FCSTD DOCUMENT  (FreeCAD 0.14R3702 (Git))
Label: battery-holder-8-AAA
License: CC-BY 3.0
LicenseURL: http://creativecommons.org/licenses/by/3.0/
objects: Part::Feature×54, Sketcher::SketchObject×25, PartDesign::Pocket×14, Part::Sweep×13, Part::Part2DObjectPython×11, Part::Compound×9, PartDesign::Pad×7, Part::MultiFuse×7, App::DocumentObjectGroup×6, Part::Mirroring×5, Part::Chamfer×4, Part::Fillet×1, PartDesign::Revolution×1, Part::Helix×1
note: 174 computed .brp shape members not serialized (recipe doc carries the construction recipe); baked Part::Feature solids carry a one-line shape summary decoded from their .brp

FEATURE [Sketcher::SketchObject] Sketch  label="battery-pack-left-body-1-sketch"
  Placement = pos=(0,0,0) rot=(1,0,0;1.5708rad)
  sketch-geometry (5):
    g0: LineSegment StartX=-19.65 StartY=11.95 StartZ=0 EndX=0 EndY=11.95 EndZ=0
    g1: LineSegment StartX=0 StartY=0 StartZ=0 EndX=-25.15 EndY=0 EndZ=0
    g2: LineSegment StartX=-25.15 StartY=0 StartZ=0 EndX=-25.15 EndY=6.45 EndZ=0
    g3: ArcOfCircle CenterX=-19.65 CenterY=6.45 CenterZ=0 NormalX=0 NormalY=0 NormalZ=1 Radius=5.5 StartAngle=1.5708 EndAngle=3.14159
    g4: LineSegment StartX=0 StartY=11.95 StartZ=0 EndX=0 EndY=0 EndZ=0
  constraints (15):
    c: Coincident(g1,g2)
    c: Horizontal(g0)
    c: Horizontal(g1)
    c: Vertical(g2)
    c: Tangent(g0,g3)
    c: Tangent(g2,g3)
    c: DistanceX(g1) = -25.15
    c: Radius(g3) = 5.5
    c: DistanceY(g-1,g0) = 11.95
    c: PointOnObject(g0,g-2)
    c: PointOnObject(g1,g-1)
    c: Coincident(g1,g-1)
    c: Vertical(g4)
    c: Coincident(g4,g0)
    c: Coincident(g4,g-1)
FEATURE [PartDesign::Pad] Pad  label="battery-pack-left-body-1"
  Length = 53.3
  Length2 = 100
  Midplane = true
  Placement = pos=(0,0,0) rot=(1,0,0;1.5708rad)
  Sketch = -> Sketch
  Type = 0
FEATURE [Sketcher::SketchObject] Sketch001  label="battery-pack-left-body-2-sketch"
  ExternalGeometry = -> [Pad]
  Placement = pos=(0,0,11.95) rot=(0,0,1;3.14159rad)
  Support = -> Pad [Face1]
  sketch-geometry (21):
    g0: LineSegment StartX=0.575 StartY=24.85 StartZ=0 EndX=11.6875 EndY=24.85 EndZ=0
    g1: LineSegment StartX=11.6875 StartY=24.85 StartZ=0 EndX=11.6875 EndY=-24.85 EndZ=0
    g2: LineSegment StartX=11.6875 StartY=-24.85 StartZ=0 EndX=0.575 EndY=-24.85 EndZ=0
    g3: LineSegment StartX=0.575 StartY=-24.85 StartZ=0 EndX=0.575 EndY=24.85 EndZ=0
    g4: LineSegment StartX=12.8375 StartY=24.85 StartZ=0 EndX=23.95 EndY=24.85 EndZ=0
    g5: LineSegment StartX=23.95 StartY=24.85 StartZ=0 EndX=23.95 EndY=22.75 EndZ=0
    g6: LineSegment StartX=23.95 StartY=-24.85 StartZ=0 EndX=12.8375 EndY=-24.85 EndZ=0
    g7: LineSegment StartX=12.8375 StartY=-24.85 StartZ=0 EndX=12.8375 EndY=24.85 EndZ=0
    g8: LineSegment [constr] StartX=12.2625 StartY=24.85 StartZ=0 EndX=12.2625 EndY=-24.85 EndZ=0
    g9: LineSegment StartX=22.75 StartY=22.75 StartZ=0 EndX=23.95 EndY=22.75 EndZ=0
    g10: LineSegment StartX=21.55 StartY=21.55 StartZ=0 EndX=21.55 EndY=10.15 EndZ=0
    g11: LineSegment StartX=22.75 StartY=8.95 StartZ=0 EndX=23.95 EndY=8.95 EndZ=0
    g12: LineSegment StartX=23.95 StartY=8.95 StartZ=0 EndX=23.95 EndY=-8.95 EndZ=0
    g13: ArcOfCircle CenterX=22.75 CenterY=21.55 CenterZ=0 NormalX=0 NormalY=0 NormalZ=1 Radius=1.2 StartAngle=1.5708 EndAngle=3.14159
    g14: ArcOfCircle CenterX=22.75 CenterY=10.15 CenterZ=0 NormalX=0 NormalY=0 NormalZ=1 Radius=1.2 StartAngle=3.14159 EndAngle=4.71239
    g15: LineSegment StartX=23.95 StartY=-8.95 StartZ=0 EndX=22.75 EndY=-8.95 EndZ=0
    g16: LineSegment StartX=21.55 StartY=-10.15 StartZ=0 EndX=21.55 EndY=-21.55 EndZ=0
    g17: LineSegment StartX=22.75 StartY=-22.75 StartZ=0 EndX=23.95 EndY=-22.75 EndZ=0
    g18: LineSegment StartX=23.95 StartY=-22.75 StartZ=0 EndX=23.95 EndY=-24.85 EndZ=0
    g19: ArcOfCircle CenterX=22.75 CenterY=-10.15 CenterZ=0 NormalX=0 NormalY=0 NormalZ=1 Radius=1.2 StartAngle=1.5708 EndAngle=3.14159
    g20: ArcOfCircle CenterX=22.75 CenterY=-21.55 CenterZ=0 NormalX=0 NormalY=0 NormalZ=1 Radius=1.2 StartAngle=3.14159 EndAngle=4.71239
  constraints (57):
    c: Coincident(g0,g1)
    c: Coincident(g1,g2)
    c: Coincident(g2,g3)
    c: Coincident(g3,g0)
    c: Horizontal(g0)
    c: Horizontal(g2)
    c: Vertical(g1)
    c: Vertical(g3)
    c: Coincident(g4,g5)
    c: Coincident(g18,g6)
    c: Coincident(g6,g7)
    c: Coincident(g7,g4)
    c: Horizontal(g4)
    c: Horizontal(g6)
    c: Vertical(g5)
    c: Vertical(g7)
    c: PointOnObject(g0,g4)
    c: Symmetric(g0,g2,g-1)
    c: PointOnObject(g1,g6)
    c: DistanceX(g-1,g0) = 0.575
    c: DistanceY(g0,g-3) = 1.8
    c: DistanceX(g4,g-4) = 1.2
    c: DistanceX(g0,g4) = 1.15
    c: PointOnObject(g8,g0)
    c: PointOnObject(g8,g2)
    c: Symmetric(g0,g4,g8)
    c: Symmetric(g0,g4,g8)
    c: Horizontal(g9)
    c: Vertical(g10)
    c: Horizontal(g11)
    c: Coincident(g5,g9)
    c: Coincident(g12,g11)
    c: Tangent(g5,g12)
    c: Tangent(g9,g13)
    c: Tangent(g10,g13)
    c: Radius(g13) = 1.2
    c: DistanceX(g10,g5) = 2.4
    c: Tangent(g10,g14)
    c: Tangent(g11,g14)
    c: Equal(g13,g14)
    c: Horizontal(g15)
    c: Vertical(g16)
    c: Horizontal(g17)
    c: Coincident(g12,g15)
    c: Coincident(g18,g17)
    c: Tangent(g12,g18)
    c: Tangent(g15,g19)
    c: Tangent(g16,g19)
    c: Tangent(g16,g20)
    c: Tangent(g17,g20)
    c: Equal(g19,g20)
    c: Equal(g20,g14)
    c: PointOnObject(g16,g10)
    c: Symmetric(g12,g11,g-1)
    c: Symmetric(g17,g5,g-1)
    c: DistanceY(g5) = -2.1
    c: DistanceY(g5,g11) = -13.8
FEATURE [PartDesign::Pocket] Pocket  label="battery-pack-left-body-2"
  Length = 10.5
  Placement = pos=(0,0,0) rot=(1,0,0;1.5708rad)
  Sketch = -> Sketch001
  Type = 0
FEATURE [Sketcher::SketchObject] Sketch002  label="left-body-3-sketch"
  ExternalGeometry = -> [Pocket]
  Placement = pos=(0,-22.75,0) rot=(1,0,0;1.5708rad)
  Support = -> Pocket [Face16]
  sketch-geometry (5):
    g0: ArcOfCircle CenterX=-15.7317 CenterY=4.18544 CenterZ=0 NormalX=0 NormalY=0 NormalZ=1 Radius=8.864 StartAngle=2.28682 EndAngle=2.75753
    g1: LineSegment [constr] StartX=-23.95 StartY=9.87929 StartZ=0 EndX=-23.95 EndY=7.50669 EndZ=0
    g2: LineSegment StartX=-23.95 StartY=7.50669 StartZ=0 EndX=-23.95 EndY=1.45 EndZ=0
    g3: LineSegment StartX=-23.95 StartY=1.45 StartZ=0 EndX=-21.55 EndY=1.45 EndZ=0
    g4: LineSegment StartX=-21.55 StartY=1.45 StartZ=0 EndX=-21.55 EndY=10.8726 EndZ=0
  constraints (13):
    c: PointOnObject(g0,g-5)
    c: Vertical(g1)
    c: Coincident(g1,g-4)
    c: Coincident(g0,g1)
    c: Vertical(g2)
    c: Coincident(g2,g3)
    c: Horizontal(g3)
    c: Coincident(g3,g4)
    c: Vertical(g4)
    c: Coincident(g4,g0)
    c: Coincident(g3,g-5)
    c: Coincident(g2,g-3)
    c: Coincident(g2,g0)
FEATURE [PartDesign::Pocket] Pocket001  label="left-body-3"
  Length = 47
  Placement = pos=(0,0,0) rot=(1,0,0;1.5708rad)
  Sketch = -> Sketch002
  Type = 0
FEATURE [Sketcher::SketchObject] Sketch003  label="left-body-4-sketch"
  ExternalGeometry = -> [Pocket001]
  Placement = pos=(-25.15,0,0) rot=(0.707107,0,-0.707107;3.14159rad)
  Support = -> Pocket001 [Face14]
  sketch-geometry (13):
    g0: LineSegment StartX=-9.87929 StartY=24.85 StartZ=0 EndX=-7.8 EndY=24.85 EndZ=0
    g1: LineSegment StartX=-6.9 StartY=23.95 StartZ=0 EndX=-6.9 EndY=23.65 EndZ=0
    g2: LineSegment StartX=-7.8 StartY=22.75 StartZ=0 EndX=-9.87929 EndY=22.75 EndZ=0
    g3: LineSegment StartX=-9.87929 StartY=22.75 StartZ=0 EndX=-9.87929 EndY=24.85 EndZ=0
    g4: ArcOfCircle CenterX=-7.8 CenterY=23.95 CenterZ=0 NormalX=0 NormalY=0 NormalZ=1 Radius=0.9 StartAngle=0 EndAngle=1.5708
    g5: ArcOfCircle CenterX=-7.8 CenterY=23.65 CenterZ=0 NormalX=0 NormalY=0 NormalZ=1 Radius=0.9 StartAngle=4.71239 EndAngle=6.28319
    g6: LineSegment StartX=-9.87929 StartY=-22.75 StartZ=0 EndX=-7.8 EndY=-22.75 EndZ=0
    g7: LineSegment StartX=-6.9 StartY=-23.65 StartZ=0 EndX=-6.9 EndY=-23.95 EndZ=0
    g8: LineSegment StartX=-7.8 StartY=-24.85 StartZ=0 EndX=-9.87929 EndY=-24.85 EndZ=0
    g9: LineSegment StartX=-9.87929 StartY=-24.85 StartZ=0 EndX=-9.87929 EndY=-22.75 EndZ=0
    g10: ArcOfCircle CenterX=-7.8 CenterY=-23.65 CenterZ=0 NormalX=0 NormalY=0 NormalZ=1 Radius=0.9 StartAngle=0 EndAngle=1.5708
    g11: ArcOfCircle CenterX=-7.8 CenterY=-23.95 CenterZ=0 NormalX=0 NormalY=0 NormalZ=1 Radius=0.9 StartAngle=4.71239 EndAngle=6.28319
    g12: LineSegment StartX=-6.45 StartY=7.15 StartZ=0 EndX=-6.45 EndY=-7.15002 EndZ=0
  constraints (32):
    c: Coincident(g2,g3)
    c: Coincident(g3,g0)
    c: Horizontal(g0)
    c: Horizontal(g2)
    c: Vertical(g1)
    c: Vertical(g3)
    c: Coincident(g0,g-3)
    c: Coincident(g2,g-3)
    c: Tangent(g0,g4)
    c: Tangent(g1,g4)
    c: Tangent(g1,g5)
    c: Tangent(g2,g5)
    c: Equal(g5,g4)
    c: Radius(g4) = 0.9
    c: DistanceX(g1,g-4) = 6.9
    c: PointOnObject(g12,g-5)
    c: Coincident(g8,g9)
    c: Coincident(g9,g6)
    c: Horizontal(g6)
    c: Horizontal(g8)
    c: Vertical(g7)
    c: Vertical(g9)
    c: Coincident(g6,g-6)
    c: Coincident(g8,g-6)
    c: Tangent(g6,g10)
    c: Tangent(g7,g10)
    c: Tangent(g7,g11)
    c: Tangent(g8,g11)
    c: Equal(g11,g10)
    c: Radius(g10) = 0.9
    c: PointOnObject(g7,g1)
    c: Vertical(g12)
FEATURE [PartDesign::Pocket] Pocket002  label="left-body-4"
  Length = 5
  Placement = pos=(0,0,0) rot=(1,0,0;1.5708rad)
  Sketch = -> Sketch003
  Type = 0
FEATURE [Sketcher::SketchObject] Sketch004  label="left-body-5-sketch"
  ExternalGeometry = -> [Pocket002]
  Placement = pos=(-25.15,0,0) rot=(0.707107,0,-0.707107;3.14159rad)
  Support = -> Pocket002 [Face12]
  sketch-geometry (6):
    g0: LineSegment StartX=-9.87929 StartY=8.95 StartZ=0 EndX=-8.25 EndY=8.95 EndZ=0
    g1: LineSegment StartX=-6.45 StartY=7.15 StartZ=0 EndX=-6.45 EndY=-7.15 EndZ=0
    g2: LineSegment StartX=-8.25 StartY=-8.95 StartZ=0 EndX=-9.87929 EndY=-8.95 EndZ=0
    g3: LineSegment StartX=-9.87929 StartY=-8.95 StartZ=0 EndX=-9.87929 EndY=8.95 EndZ=0
    g4: ArcOfCircle CenterX=-8.25 CenterY=7.15 CenterZ=0 NormalX=0 NormalY=0 NormalZ=1 Radius=1.8 StartAngle=0 EndAngle=1.5708
    g5: ArcOfCircle CenterX=-8.25 CenterY=-7.15 CenterZ=0 NormalX=0 NormalY=0 NormalZ=1 Radius=1.8 StartAngle=4.71239 EndAngle=6.28319
  constraints (15):
    c: Coincident(g2,g3)
    c: Coincident(g3,g0)
    c: Horizontal(g0)
    c: Horizontal(g2)
    c: Vertical(g1)
    c: Vertical(g3)
    c: Tangent(g0,g4)
    c: Tangent(g1,g4)
    c: Tangent(g1,g5)
    c: Tangent(g2,g5)
    c: Equal(g4,g5)
    c: Radius(g4) = 1.8
    c: PointOnObject(g1,g-3)
    c: Coincident(g0,g-4)
    c: Coincident(g2,g-4)
FEATURE [PartDesign::Pocket] Pocket003  label="left-body-5"
  Length = 5
  Midplane = true
  Placement = pos=(0,0,0) rot=(1,0,0;1.5708rad)
  Sketch = -> Sketch004
  Type = 0
FEATURE [Sketcher::SketchObject] Sketch005  label="left-body-6-sketch"
  ExternalGeometry = -> [Pocket003]
  Placement = pos=(-12.8375,0,0) rot=(0.707107,0,-0.707107;3.14159rad)
  Support = -> Pocket003 [Face7]
  sketch-geometry (4):
    g0: LineSegment StartX=-11.95 StartY=24.85 StartZ=0 EndX=-11.95 EndY=-24.85 EndZ=0
    g1: LineSegment StartX=-11.95 StartY=24.85 StartZ=0 EndX=-4.45 EndY=6.35 EndZ=0
    g2: LineSegment StartX=-4.45 StartY=6.35 StartZ=0 EndX=-4.45 EndY=-6.35 EndZ=0
    g3: LineSegment StartX=-4.45 StartY=-6.35 StartZ=0 EndX=-11.95 EndY=-24.85 EndZ=0
  constraints (11):
    c: Vertical(g0)
    c: Coincident(g1,g-3)
    c: Coincident(g1,g2)
    c: Vertical(g2)
    c: Coincident(g2,g3)
    c: Coincident(g3,g-3)
    c: Symmetric(g2,g1,g-1)
    c: DistanceX(g1,g-4) = 3
    c: DistanceY(g-4,g1) = -18.5
    c: Coincident(g0,g1)
    c: Coincident(g0,g3)
FEATURE [PartDesign::Pocket] Pocket004  label="left-body-6"
  Length = 5
  Placement = pos=(0,0,0) rot=(1,0,0;1.5708rad)
  Sketch = -> Sketch005
  Type = 1
FEATURE [Sketcher::SketchObject] Sketch006  label="left-body-7-sketch"
  ExternalGeometry = -> [Pocket004]
  Placement = pos=(0,-26.65,0) rot=(1,0,0;1.5708rad)
  Support = -> Pocket004 [Face11]
  sketch-geometry (4):
    g0: LineSegment [constr] StartX=-18.3937 StartY=6.65 StartZ=0 EndX=-18.3937 EndY=1.45 EndZ=0
    g1: Circle CenterX=-18.3937 CenterY=6.65 CenterZ=0 NormalX=0 NormalY=0 NormalZ=1 Radius=3.45
    g2: LineSegment [constr] StartX=-6.13125 StartY=6.65 StartZ=0 EndX=-6.13125 EndY=1.45 EndZ=0
    g3: Circle CenterX=-6.13125 CenterY=6.65 CenterZ=0 NormalX=0 NormalY=0 NormalZ=1 Radius=3.45
  constraints (12):
    c: Vertical(g0)
    c: PointOnObject(g0,g-5)
    c: Symmetric(g-5,g-5,g0)
    c: Coincident(g1,g0)
    c: Radius(g1) = 3.45
    c: DistanceY(g0) = -5.2
    c: Vertical(g2)
    c: PointOnObject(g2,g-8)
    c: Equal(g2,g0)
    c: Coincident(g3,g2)
    c: Equal(g3,g1)
    c: Symmetric(g-8,g-8,g2)
FEATURE [PartDesign::Pocket] Pocket005  label="left-body-7"
  Length = 0.86
  Placement = pos=(0,0,0) rot=(1,0,0;1.5708rad)
  Sketch = -> Sketch006
  Type = 0
FEATURE [Sketcher::SketchObject] Sketch007  label="left-body-8-sketch"
  ExternalGeometry = -> [Pocket005]
  Placement = pos=(0,26.65,0) rot=(-1,0,0;1.5708rad)
  Support = -> Pocket005 [Face2]
  sketch-geometry (4):
    g0: LineSegment [constr] StartX=-18.3937 StartY=-1.45 StartZ=0 EndX=-18.3937 EndY=-6.65 EndZ=0
    g1: LineSegment [constr] StartX=-6.13125 StartY=-1.45 StartZ=0 EndX=-6.13125 EndY=-6.65 EndZ=0
    g2: Circle CenterX=-18.3937 CenterY=-6.65 CenterZ=0 NormalX=0 NormalY=0 NormalZ=1 Radius=3.45
    g3: Circle CenterX=-6.13125 CenterY=-6.65 CenterZ=0 NormalX=0 NormalY=0 NormalZ=1 Radius=3.45
  constraints (12):
    c: Vertical(g0)
    c: PointOnObject(g0,g-3)
    c: Vertical(g1)
    c: PointOnObject(g1,g-4)
    c: Symmetric(g-6,g-5,g0)
    c: Symmetric(g-7,g-8,g1)
    c: Equal(g0,g1)
    c: DistanceY(g0) = -5.2
    c: Equal(g3,g2)
    c: Coincident(g0,g2)
    c: Coincident(g3,g1)
    c: Radius(g2) = 3.45
FEATURE [PartDesign::Pocket] Pocket006  label="left-body-8"
  Length = 0.86
  Placement = pos=(0,0,0) rot=(1,0,0;1.5708rad)
  Sketch = -> Sketch007
  Type = 0
FEATURE [Sketcher::SketchObject] Sketch008  label="left-body-9-sketch"
  ExternalGeometry = -> [Pocket006]
  Placement = pos=(0,-26.65,0) rot=(1,0,0;1.5708rad)
  Support = -> Pocket006 [Face13]
  sketch-geometry (9):
    g0: LineSegment StartX=-13.1625 StartY=8.95 StartZ=0 EndX=-11.3625 EndY=8.95 EndZ=0
    g1: LineSegment StartX=-11.3625 StartY=8.95 StartZ=0 EndX=-11.3625 EndY=2.45 EndZ=0
    g2: LineSegment StartX=-11.3625 StartY=2.45 StartZ=0 EndX=-13.1625 EndY=2.45 EndZ=0
    g3: LineSegment StartX=-13.1625 StartY=2.45 StartZ=0 EndX=-13.1625 EndY=8.95 EndZ=0
    g4: LineSegment [constr] StartX=-12.2625 StartY=11.95 StartZ=0 EndX=-12.2625 EndY=1.45 EndZ=0
    g5: LineSegment StartX=-0.9 StartY=8.95 StartZ=0 EndX=0.9 EndY=8.95 EndZ=0
    g6: LineSegment StartX=0.9 StartY=8.95 StartZ=0 EndX=0.9 EndY=2.45 EndZ=0
    g7: LineSegment StartX=0.9 StartY=2.45 StartZ=0 EndX=-0.9 EndY=2.45 EndZ=0
    g8: LineSegment StartX=-0.9 StartY=2.45 StartZ=0 EndX=-0.9 EndY=8.95 EndZ=0
  constraints (27):
    c: Coincident(g0,g1)
    c: Coincident(g1,g2)
    c: Coincident(g2,g3)
    c: Coincident(g3,g0)
    c: Horizontal(g0)
    c: Horizontal(g2)
    c: Vertical(g1)
    c: Vertical(g3)
    c: PointOnObject(g4,g-5)
    c: PointOnObject(g4,g-6)
    c: Symmetric(g-3,g-4,g4)
    c: Symmetric(g0,g0,g4)
    c: DistanceX(g0) = 1.8
    c: DistanceY(g1) = -6.5
    c: DistanceY(g0,g-3) = 3
    c: Coincident(g5,g6)
    c: Coincident(g6,g7)
    c: Coincident(g7,g8)
    c: Coincident(g8,g5)
    c: Horizontal(g5)
    c: Horizontal(g7)
    c: Vertical(g6)
    c: Vertical(g8)
    c: PointOnObject(g5,g0)
    c: Equal(g8,g1)
    c: Equal(g5,g0)
    c: Symmetric(g5,g5,g-2)
FEATURE [PartDesign::Pocket] Pocket007  label="left-body-9"
  Length = 3.4
  Placement = pos=(0,0,0) rot=(1,0,0;1.5708rad)
  Sketch = -> Sketch008
  Type = 0
FEATURE [Sketcher::SketchObject] Sketch009  label="left-body-10-sketch"
  ExternalGeometry = -> [Pocket007]
  Placement = pos=(0,26.65,0) rot=(-1,0,0;1.5708rad)
  Support = -> Pocket007 [Face2]
  sketch-geometry (8):
    g0: LineSegment StartX=-13.1625 StartY=-2.45 StartZ=0 EndX=-11.3625 EndY=-2.45 EndZ=0
    g1: LineSegment StartX=-11.3625 StartY=-2.45 StartZ=0 EndX=-11.3625 EndY=-8.95 EndZ=0
    g2: LineSegment StartX=-11.3625 StartY=-8.95 StartZ=0 EndX=-13.1625 EndY=-8.95 EndZ=0
    g3: LineSegment StartX=-13.1625 StartY=-8.95 StartZ=0 EndX=-13.1625 EndY=-2.45 EndZ=0
    g4: LineSegment StartX=-0.9 StartY=-2.45 StartZ=0 EndX=0 EndY=-2.45 EndZ=0
    g5: LineSegment StartX=0 StartY=-2.45 StartZ=0 EndX=0 EndY=-8.95 EndZ=0
    g6: LineSegment StartX=0 StartY=-8.95 StartZ=0 EndX=-0.9 EndY=-8.95 EndZ=0
    g7: LineSegment StartX=-0.9 StartY=-8.95 StartZ=0 EndX=-0.9 EndY=-2.45 EndZ=0
  constraints (21):
    c: Coincident(g0,g1)
    c: Coincident(g1,g2)
    c: Coincident(g2,g3)
    c: Coincident(g3,g0)
    c: Horizontal(g0)
    c: Horizontal(g2)
    c: Vertical(g1)
    c: Vertical(g3)
    c: Coincident(g4,g5)
    c: Coincident(g5,g6)
    c: Coincident(g6,g7)
    c: Coincident(g7,g4)
    c: Horizontal(g4)
    c: Horizontal(g6)
    c: Vertical(g5)
    c: Vertical(g7)
    c: Coincident(g0,g-3)
    c: Coincident(g1,g-4)
    c: Coincident(g4,g-5)
    c: PointOnObject(g4,g-2)
    c: Coincident(g6,g-5)
FEATURE [PartDesign::Pocket] Pocket008  label="left-body-10"
  Length = 3.4
  Placement = pos=(0,0,0) rot=(1,0,0;1.5708rad)
  Sketch = -> Sketch009
  Type = 0
FEATURE [Sketcher::SketchObject] Sketch010  label="left-body-11-side-drills-sketch"
  ExternalGeometry = -> [Pocket008]
  Placement = pos=(0,-25.79,0) rot=(1,0,0;1.5708rad)
  Support = -> Pocket008 [Face72]
  sketch-geometry (2):
    g0: Circle CenterX=-18.3937 CenterY=6.65 CenterZ=0 NormalX=0 NormalY=0 NormalZ=1 Radius=1.25
    g1: Circle CenterX=-6.13125 CenterY=6.65 CenterZ=0 NormalX=0 NormalY=0 NormalZ=1 Radius=1.25
  constraints (4):
    c: Coincident(g0,g-3)
    c: Radius(g0) = 1.25
    c: Coincident(g1,g-4)
    c: Equal(g1,g0)
FEATURE [PartDesign::Pocket] Pocket009  label="left-body-11-side-drills"
  Length = 5
  Placement = pos=(0,0,0) rot=(1,0,0;1.5708rad)
  Sketch = -> Sketch010
  Type = 1
FEATURE [Sketcher::SketchObject] Sketch011  label="left-body-12-top-drills-sketch"
  ExternalGeometry = -> [Pocket009]
  Placement = pos=(0,0,1.45) rot=(0,0,1;3.14159rad)
  Support = -> Pocket009 [Face36]
  sketch-geometry (8):
    g0: Circle CenterX=6.13125 CenterY=0 CenterZ=0 NormalX=0 NormalY=0 NormalZ=1 Radius=1.3
    g1: Circle CenterX=18.3937 CenterY=0 CenterZ=0 NormalX=0 NormalY=0 NormalZ=1 Radius=1.3
    g2: LineSegment [constr] StartX=6.13125 StartY=24.85 StartZ=0 EndX=6.13125 EndY=-24.85 EndZ=0
    g3: LineSegment [constr] StartX=18.3937 StartY=24.85 StartZ=0 EndX=18.3937 EndY=-24.85 EndZ=0
    g4: LineSegment StartX=14.8937 StartY=-22.85 StartZ=0 EndX=21.8937 EndY=-22.85 EndZ=0
    g5: LineSegment StartX=21.8937 StartY=-22.85 StartZ=0 EndX=21.8937 EndY=-24.85 EndZ=0
    g6: LineSegment StartX=21.8937 StartY=-24.85 StartZ=0 EndX=14.8937 EndY=-24.85 EndZ=0
    g7: LineSegment StartX=14.8937 StartY=-24.85 StartZ=0 EndX=14.8937 EndY=-22.85 EndZ=0
  constraints (24):
    c: PointOnObject(g0,g-1)
    c: PointOnObject(g1,g-1)
    c: Equal(g0,g1)
    c: Radius(g1) = 1.3
    c: PointOnObject(g2,g-5)
    c: PointOnObject(g2,g-6)
    c: Symmetric(g-5,g-5,g2)
    c: PointOnObject(g0,g2)
    c: PointOnObject(g3,g-7)
    c: Symmetric(g-10,g-8,g3)
    c: PointOnObject(g3,g-11)
    c: PointOnObject(g1,g3)
    c: Coincident(g4,g5)
    c: Coincident(g5,g6)
    c: Coincident(g6,g7)
    c: Coincident(g7,g4)
    c: Horizontal(g4)
    c: Horizontal(g6)
    c: Vertical(g5)
    c: Vertical(g7)
    c: DistanceX(g6) = -7
    c: DistanceY(g7) = 2
    c: PointOnObject(g6,g-11)
    c: Symmetric(g6,g5,g3)
FEATURE [PartDesign::Pocket] Pocket010  label="left-body-12-top-drills"
  Length = 5
  Placement = pos=(0,0,0) rot=(1,0,0;1.5708rad)
  Sketch = -> Sketch011
  Type = 1
FEATURE [Part::Chamfer] Chamfer001  label="left-body-13"
  Base = -> Pocket010
  Edges = 1 edges r=0.3: [Edge144]
FEATURE [Part::Fillet] Fillet
  Base = -> Chamfer001
  Edges = 9 edges r=0.3: [Edge77,Edge79,Edge127,Edge128,Edge129,Edge136,Edge160,Edge161,Edge166]
FEATURE [Part::Mirroring] Part__Mirroring  label="Fillet (Mirror #1)"
  Base = (0,0,0)
  Normal = (1,0,0)
  Source = -> Fillet
FEATURE [Part::MultiFuse] Fusion  label="top-body-1"
  Shapes = -> [Part__Mirroring,Fillet]
FEATURE [Sketcher::SketchObject] Sketch014  label="serigrafy-1-sketch"
  sketch-geometry (12):
    g0: LineSegment StartX=-2.3 StartY=9.75 StartZ=0 EndX=2.3 EndY=9.75 EndZ=0
    g1: LineSegment StartX=2.3 StartY=9.75 StartZ=0 EndX=2.3 EndY=-7.45 EndZ=0
    g2: LineSegment StartX=2.3 StartY=-7.45 StartZ=0 EndX=-2.3 EndY=-7.45 EndZ=0
    g3: LineSegment StartX=-2.3 StartY=-7.45 StartZ=0 EndX=-2.3 EndY=9.75 EndZ=0
    g4: LineSegment StartX=-2.5 StartY=9.95 StartZ=0 EndX=2.5 EndY=9.95 EndZ=0
    g5: LineSegment StartX=2.5 StartY=9.95 StartZ=0 EndX=2.5 EndY=-7.65 EndZ=0
    g6: LineSegment StartX=2.5 StartY=-7.65 StartZ=0 EndX=-2.5 EndY=-7.65 EndZ=0
    g7: LineSegment StartX=-2.5 StartY=-7.65 StartZ=0 EndX=-2.5 EndY=9.95 EndZ=0
    g8: LineSegment [constr] StartX=-1.15 StartY=-7.65 StartZ=0 EndX=-1.15 EndY=-9.75 EndZ=0
    g9: LineSegment [constr] StartX=-1.15 StartY=-9.75 StartZ=0 EndX=1.15 EndY=-9.75 EndZ=0
    g10: LineSegment [constr] StartX=1.15 StartY=-9.75 StartZ=0 EndX=1.15 EndY=-7.65 EndZ=0
    g11: LineSegment [constr] StartX=0 StartY=9.75 StartZ=0 EndX=0 EndY=-9.75 EndZ=0
  constraints (38):
    c: Coincident(g0,g1)
    c: Coincident(g1,g2)
    c: Coincident(g2,g3)
    c: Coincident(g3,g0)
    c: Horizontal(g0)
    c: Horizontal(g2)
    c: Vertical(g1)
    c: Vertical(g3)
    c: Symmetric(g0,g0,g-2)
    c: DistanceX(g0) = 4.6
    c: DistanceY(g1) = -17.2
    c: Coincident(g4,g5)
    c: Coincident(g5,g6)
    c: Coincident(g6,g7)
    c: Coincident(g7,g4)
    c: Horizontal(g4)
    c: Horizontal(g6)
    c: Vertical(g5)
    c: Vertical(g7)
    c: DistanceX(g0,g4) = 0.2
    c: DistanceY(g4,g0) = -0.2
    c: DistanceX(g2,g6) = -0.2
    c: DistanceY(g6,g2) = 0.2
    c: PointOnObject(g8,g6)
    c: Vertical(g8)
    c: Coincident(g8,g9)
    c: Horizontal(g9)
    c: Coincident(g9,g10)
    c: PointOnObject(g10,g6)
    c: Vertical(g10)
    c: Symmetric(g9,g8,g-2)
    c: Vertical(g11)
    c: PointOnObject(g11,g-2)
    c: PointOnObject(g11,g9)
    c: DistanceX(g9) = 2.3
    c: DistanceY(g10) = 2.1
    c: PointOnObject(g11,g0)
    c: Symmetric(g11,g11,g-1)
FEATURE [PartDesign::Pad] Pad001  label="serigrafy-1"
  Length = 0.1
  Length2 = 100
  Sketch = -> Sketch014
  Type = 0
FEATURE [Sketcher::SketchObject] Sketch015  label="serigrafy-2-sketch"
  ExternalGeometry = -> [Pad001]
  Placement = pos=(0,0,0) rot=(1,0,0;3.14159rad)
  Support = -> Pad001 [Face9]
  sketch-geometry (8):
    g0: LineSegment StartX=-1.15 StartY=9.75 StartZ=0 EndX=1.15 EndY=9.75 EndZ=0
    g1: LineSegment StartX=1.15 StartY=9.75 StartZ=0 EndX=1.15 EndY=7.65 EndZ=0
    g2: LineSegment StartX=-1.15 StartY=7.65 StartZ=0 EndX=-1.15 EndY=9.75 EndZ=0
    g3: LineSegment StartX=-1.35 StartY=9.95 StartZ=0 EndX=1.35 EndY=9.95 EndZ=0
    g4: LineSegment StartX=1.35 StartY=9.95 StartZ=0 EndX=1.35 EndY=7.65 EndZ=0
    g5: LineSegment StartX=-1.35 StartY=7.65 StartZ=0 EndX=-1.35 EndY=9.95 EndZ=0
    g6: LineSegment StartX=-1.35 StartY=7.65 StartZ=0 EndX=-1.15 EndY=7.65 EndZ=0
    g7: LineSegment StartX=1.15 StartY=7.65 StartZ=0 EndX=1.35 EndY=7.65 EndZ=0
  constraints (25):
    c: Coincident(g0,g1)
    c: Coincident(g2,g0)
    c: Horizontal(g0)
    c: Vertical(g1)
    c: Vertical(g2)
    c: Coincident(g3,g4)
    c: Coincident(g5,g3)
    c: Horizontal(g3)
    c: Vertical(g4)
    c: Vertical(g5)
    c: Symmetric(g3,g3,g-2)
    c: PointOnObject(g4,g-4)
    c: DistanceX(g0,g3) = 0.2
    c: DistanceY(g0,g3) = 0.2
    c: DistanceX(g0) = 2.3
    c: DistanceY(g2) = 2.1
    c: PointOnObject(g2,g-4)
    c: PointOnObject(g1,g-4)
    c: Horizontal(g6)
    c: Coincident(g6,g2)
    c: Horizontal(g7)
    c: Coincident(g7,g4)
    c: Coincident(g7,g1)
    c: Coincident(g6,g5)
    c: DistanceX(g0,g3) = -0.2
FEATURE [PartDesign::Pad] Pad002  label="serigrafy-2"
  Length = 0.1
  Length2 = 100
  Reversed = true
  Sketch = -> Sketch015
  Type = 0
FEATURE [Sketcher::SketchObject] Sketch016  label="serigrafy-3-sketch"
  sketch-geometry (4):
    g0: Circle CenterX=0 CenterY=-13.56 CenterZ=0 NormalX=0 NormalY=0 NormalZ=1 Radius=2.125
    g1: Circle CenterX=0 CenterY=-13.56 CenterZ=0 NormalX=0 NormalY=0 NormalZ=1 Radius=2.325
    g2: Circle CenterX=0 CenterY=13.56 CenterZ=0 NormalX=0 NormalY=0 NormalZ=1 Radius=2.125
    g3: Circle CenterX=0 CenterY=13.56 CenterZ=0 NormalX=0 NormalY=0 NormalZ=1 Radius=2.325
  constraints (10):
    c: PointOnObject(g0,g-2)
    c: Radius(g0) = 2.125
    c: Coincident(g1,g0)
    c: Radius(g1) = 2.325
    c: DistanceY(g-1,g0) = -13.56
    c: PointOnObject(g2,g-2)
    c: Coincident(g3,g2)
    c: Equal(g2,g0)
    c: Equal(g1,g3)
    c: Symmetric(g2,g0,g-1)
FEATURE [PartDesign::Pad] Pad003  label="serigrafy-3"
  Length = 0.1
  Length2 = 100
  Sketch = -> Sketch016
  Type = 0
FEATURE [Sketcher::SketchObject] Sketch017  label="serigraf-4-sketch"
  sketch-geometry (15):
    g0: Circle [constr] CenterX=0 CenterY=-13.56 CenterZ=0 NormalX=0 NormalY=0 NormalZ=1 Radius=2
    g1: LineSegment [constr] StartX=-1.6 StartY=-13.56 StartZ=0 EndX=1.6 EndY=-13.56 EndZ=0
    g2: LineSegment [constr] StartX=0 StartY=-11.96 StartZ=0 EndX=0 EndY=-15.16 EndZ=0
    g3: LineSegment StartX=-0.1 StartY=-11.96 StartZ=0 EndX=0.1 EndY=-11.96 EndZ=0
    g4: LineSegment StartX=0.1 StartY=-11.96 StartZ=0 EndX=0.1 EndY=-13.46 EndZ=0
    g5: LineSegment StartX=0.1 StartY=-15.16 StartZ=0 EndX=-0.1 EndY=-15.16 EndZ=0
    g6: LineSegment StartX=-0.1 StartY=-15.16 StartZ=0 EndX=-0.1 EndY=-13.66 EndZ=0
    g7: LineSegment StartX=-1.6 StartY=-13.46 StartZ=0 EndX=-0.1 EndY=-13.46 EndZ=0
    g8: LineSegment StartX=1.6 StartY=-13.46 StartZ=0 EndX=1.6 EndY=-13.66 EndZ=0
    g9: LineSegment StartX=1.6 StartY=-13.66 StartZ=0 EndX=0.1 EndY=-13.66 EndZ=0
    g10: LineSegment StartX=-1.6 StartY=-13.66 StartZ=0 EndX=-1.6 EndY=-13.46 EndZ=0
    g11: LineSegment StartX=-0.1 StartY=-13.46 StartZ=0 EndX=-0.1 EndY=-11.96 EndZ=0
    g12: LineSegment StartX=-0.1 StartY=-13.66 StartZ=0 EndX=-1.6 EndY=-13.66 EndZ=0
    g13: LineSegment StartX=0.1 StartY=-13.66 StartZ=0 EndX=0.1 EndY=-15.16 EndZ=0
    g14: LineSegment StartX=0.1 StartY=-13.46 StartZ=0 EndX=1.6 EndY=-13.46 EndZ=0
  constraints (40):
    c: Radius(g0) = 2
    c: DistanceY(g-1,g0) = -13.56
    c: PointOnObject(g0,g-2)
    c: PointOnObject(g0,g1)
    c: Symmetric(g1,g1,g-2)
    c: Vertical(g2)
    c: Symmetric(g2,g2,g1)
    c: Equal(g2,g1)
    c: PointOnObject(g2,g-2)
    c: Coincident(g3,g4)
    c: Coincident(g13,g5)
    c: Coincident(g5,g6)
    c: Coincident(g11,g3)
    c: Horizontal(g3)
    c: Horizontal(g5)
    c: Vertical(g4)
    c: Vertical(g6)
    c: Coincident(g14,g8)
    c: Coincident(g8,g9)
    c: Coincident(g12,g10)
    c: Coincident(g10,g7)
    c: Horizontal(g7)
    c: Horizontal(g9)
    c: Vertical(g8)
    c: Vertical(g10)
    c: Symmetric(g3,g13,g0)
    c: Symmetric(g7,g8,g0)
    c: PointOnObject(g1,g10)
    c: PointOnObject(g2,g3)
    c: Tangent(g6,g11)
    c: Coincident(g12,g6)
    c: Tangent(g9,g12)
    c: Coincident(g13,g9)
    c: Tangent(g4,g13)
    c: Coincident(g14,g4)
    c: Tangent(g7,g14)
    c: Coincident(g7,g11)
    c: Equal(g10,g3)
    c: DistanceY(g2) = -3.2
    c: DistanceY(g8) = -0.2
FEATURE [PartDesign::Pad] Pad004  label="serigrafy-4"
  Length = 0.1
  Length2 = 100
  Sketch = -> Sketch017
  Type = 0
FEATURE [Sketcher::SketchObject] Sketch018  label="serigrafy-5-sketch"
  sketch-geometry (5):
    g0: LineSegment [constr] StartX=0 StartY=13.56 StartZ=0 EndX=0 EndY=0 EndZ=0
    g1: LineSegment StartX=-0.1 StartY=15.16 StartZ=0 EndX=0.1 EndY=15.16 EndZ=0
    g2: LineSegment StartX=0.1 StartY=15.16 StartZ=0 EndX=0.1 EndY=11.96 EndZ=0
    g3: LineSegment StartX=0.1 StartY=11.96 StartZ=0 EndX=-0.1 EndY=11.96 EndZ=0
    g4: LineSegment StartX=-0.1 StartY=11.96 StartZ=0 EndX=-0.1 EndY=15.16 EndZ=0
  constraints (14):
    c: Coincident(g0,g-1)
    c: Vertical(g0)
    c: DistanceY(g0) = -13.56
    c: Coincident(g1,g2)
    c: Coincident(g2,g3)
    c: Coincident(g3,g4)
    c: Coincident(g4,g1)
    c: Horizontal(g1)
    c: Horizontal(g3)
    c: Vertical(g2)
    c: Vertical(g4)
    c: Symmetric(g1,g2,g0)
    c: DistanceY(g2) = -3.2
    c: DistanceX(g1) = 0.2
FEATURE [PartDesign::Pad] Pad005  label="serigrafy-5"
  Length = 0.1
  Length2 = 100
  Sketch = -> Sketch018
  Type = 0
FEATURE [Part::MultiFuse] Fusion001  label="battery-1-serigrafy"
  Placement = pos=(-18.45,0,0) rot=(0,0,1;0rad)
  Shapes = -> [Pad001,Pad005,Pad002,Pad004,Pad003]
FEATURE [Part::Feature] Fusion001001  label="battery-2-serigrafy"
  Placement = pos=(6,0,0) rot=(0,0,1;0rad)
  shape: bbox 5 x 31.77 x 0.1 mm, 46 faces, 5 solids (baked)
FEATURE [Part::Feature] Fusion001001001  label="battery-3-serigrafy"
  Placement = pos=(-6,0,0) rot=(0,0,1;3.14159rad)
  shape: bbox 5 x 31.77 x 0.1 mm, 46 faces, 5 solids (baked)
FEATURE [Part::Feature] Fusion001001001001  label="battery-4-serigrafy"
  Placement = pos=(18.45,0,0) rot=(0,0,1;3.14159rad)
  shape: bbox 5 x 31.77 x 0.1 mm, 46 faces, 5 solids (baked)
FEATURE [Part::MultiFuse] Fusion001001001002  label="Battery-serigrafy-final"
  Placement = pos=(0,0,1.45) rot=(0,0,1;0rad)
  Shapes = -> [Fusion001,Fusion001001,Fusion001001001,Fusion001001001001]
FEATURE [Sketcher::SketchObject] Sketch019  label="quarter-star-sketch"
  Placement = pos=(0,0,0) rot=(1,0,0;1.5708rad)
  sketch-geometry (9):
    g0: LineSegment StartX=-2.50933 StartY=0.525 StartZ=0 EndX=-0.909327 EndY=0.525 EndZ=0
    g1: LineSegment StartX=0 StartY=0 StartZ=0 EndX=-2.50933 EndY=0 EndZ=0
    g2: LineSegment StartX=-2.50933 StartY=0 StartZ=0 EndX=-2.50933 EndY=0.525 EndZ=0
    g3: LineSegment [constr] StartX=-1.25466 StartY=2.17314 StartZ=0 EndX=0 EndY=0 EndZ=0
    g4: LineSegment [constr] StartX=-0.909327 StartY=0.525 StartZ=0 EndX=0 EndY=0 EndZ=0
    g5: LineSegment StartX=-0.909327 StartY=0.525 StartZ=0 EndX=-1.70933 EndY=1.91064 EndZ=0
    g6: LineSegment StartX=-1.70933 StartY=1.91064 StartZ=0 EndX=-0.8 EndY=2.43564 EndZ=0
    g7: LineSegment StartX=-0.8 StartY=2.43564 StartZ=0 EndX=0 EndY=1.05 EndZ=0
    g8: LineSegment StartX=0 StartY=1.05 StartZ=0 EndX=0 EndY=0 EndZ=0
  constraints (27):
    c: Coincident(g1,g2)
    c: Coincident(g2,g0)
    c: Horizontal(g0)
    c: Horizontal(g1)
    c: Vertical(g2)
    c: Coincident(g3,g-1)
    c: Angle(g-1,g3) = 2.0944
    c: Coincident(g4,g-1)
    c: Angle(g-1,g4) = 2.61799
    c: PointOnObject(g1,g-1)
    c: Coincident(g5,g6)
    c: Coincident(g6,g7)
    c: PointOnObject(g7,g-2)
    c: Parallel(g5,g3)
    c: Perpendicular(g6,g3)
    c: DistanceX(g0) = 1.6
    c: Equal(g0,g5)
    c: PointOnObject(g3,g6)
    c: Parallel(g7,g3)
    c: Distance(g4) = 1.05
    c: Coincident(g-1,g1)
    c: Vertical(g8)
    c: Coincident(g7,g8)
    c: Coincident(g8,g-1)
    c: Equal(g8,g4)
    c: Coincident(g0,g4)
    c: Coincident(g5,g0)
FEATURE [PartDesign::Pad] Pad006  label="quarter-star"
  Length = 0.2
  Length2 = 100
  Placement = pos=(0,0,0) rot=(1,0,0;1.5708rad)
  Sketch = -> Sketch019
  Type = 0
FEATURE [Part::Mirroring] Part__Mirroring001  label="quarter-star (Mirror #2)"
  Base = (0,0,0)
  Normal = (1,0,0)
  Source = -> Pad006
FEATURE [Part::MultiFuse] Fusion001001001003004  label="top-half-star"
  Shapes = -> [Part__Mirroring001,Pad006]
FEATURE [Part::Mirroring] Part__Mirroring002  label="top-half-star (Mirror #3)"
  Base = (0,0,0)
  Normal = (0,0,1)
  Source = -> Fusion001001001003004
FEATURE [Part::MultiFuse] Fusion001001001003005  label="contact-star-body"
  Shapes = -> [Part__Mirroring002,Fusion001001001003004]
FEATURE [Sketcher::SketchObject] Sketch020  label="star-drill-sketch"
  Placement = pos=(0,-0.2,0) rot=(1,0,0;1.5708rad)
  Support = -> Fusion001001001003005 [Face19]
  sketch-geometry (1):
    g0: Circle CenterX=0 CenterY=0 CenterZ=0 NormalX=0 NormalY=0 NormalZ=1 Radius=0.9
  constraints (1):
    c: Radius(g0) = 0.9
FEATURE [Part::Feature] Pocket014  label="star-1"
  Placement = pos=(-6.73125,-25.79,5.7) rot=(0,0,1;0rad)
  shape: bbox 5.019 x 0.2 x 4.871 mm, 21 faces (baked)
FEATURE [Part::Feature] Pocket015  label="star-2"
  Placement = pos=(-18.9937,-25.79,5.7) rot=(0,0,1;0rad)
  shape: bbox 5.019 x 0.2 x 4.871 mm, 21 faces (baked)
FEATURE [Part::Feature] Pocket016  label="star-3"
  Placement = pos=(5.53125,-25.79,5.7) rot=(0,0,1;0rad)
  shape: bbox 5.019 x 0.2 x 4.871 mm, 21 faces (baked)
FEATURE [Part::Feature] Pocket017  label="star-004"
  Placement = pos=(17.7937,-25.79,-7.6) rot=(0,0,1;0rad)
  shape: bbox 5.019 x 0.2 x 4.871 mm, 21 faces (baked)
FEATURE [Part::Feature] Pocket018  label="star-005"
  Placement = pos=(-6.73125,-25.79,-7.6) rot=(0,0,1;0rad)
  shape: bbox 5.019 x 0.2 x 4.871 mm, 21 faces (baked)
FEATURE [Part::Feature] Pocket019  label="star-006"
  Placement = pos=(17.7937,25.79,5.7) rot=(0,0,1;3.14159rad)
  shape: bbox 5.019 x 0.2 x 4.871 mm, 21 faces (baked)
FEATURE [PartDesign::Pocket] Pocket013  label="contact-star-final"
  Length = 5
  Sketch = -> Sketch020
  Type = 1
FEATURE [Part::Feature] Pocket020  label="star-007"
  Placement = pos=(5.53125,25.79,-7.6) rot=(0,0,1;3.14159rad)
  shape: bbox 5.019 x 0.2 x 4.871 mm, 21 faces (baked)
FEATURE [Part::Feature] Pocket021  label="star-008"
  Placement = pos=(-6.73125,25.79,5.7) rot=(0,0,1;3.14159rad)
  shape: bbox 5.019 x 0.2 x 4.871 mm, 21 faces (baked)
FEATURE [Part::Feature] Pocket022  label="star-009"
  Placement = pos=(-18.9937,25.79,-7.6) rot=(0,0,1;3.14159rad)
  shape: bbox 5.019 x 0.2 x 4.871 mm, 21 faces (baked)
FEATURE [Part::Compound] Compound  label="contact-stars"
  Links = -> [Pocket014,Pocket017,Pocket016,Pocket018,Pocket015,Pocket019,Pocket021,Pocket022,Pocket020]
FEATURE [Sketcher::SketchObject] Sketch021  label="contact-1-sketch"
  sketch-geometry (6):
    g0: LineSegment StartX=0.8 StartY=0 StartZ=0 EndX=1.9 EndY=0 EndZ=0
    g1: LineSegment StartX=1.9 StartY=0 StartZ=0 EndX=1.9 EndY=0.75 EndZ=0
    g2: LineSegment StartX=0.8 StartY=0.75 StartZ=0 EndX=0.8 EndY=0 EndZ=0
    g3: ArcOfCircle CenterX=1.35 CenterY=0.75 CenterZ=0 NormalX=0 NormalY=0 NormalZ=1 Radius=0.55 StartAngle=0 EndAngle=3.14159
    g4: LineSegment [constr] StartX=0.8 StartY=0.75 StartZ=0 EndX=1.9 EndY=0.75 EndZ=0
    g5: LineSegment [constr] StartX=1.35 StartY=1.3 StartZ=0 EndX=1.35 EndY=0 EndZ=0
  constraints (19):
    c: Coincident(g0,g1)
    c: Horizontal(g0)
    c: Vertical(g1)
    c: Vertical(g2)
    c: Coincident(g2,g0)
    c: PointOnObject(g0,g-1)
    c: DistanceX(g-1,g0) = 0.8
    c: DistanceX(g-1,g0) = 1.9
    c: Horizontal(g4)
    c: Coincident(g4,g2)
    c: Coincident(g4,g1)
    c: PointOnObject(g3,g4)
    c: Coincident(g3,g2)
    c: Coincident(g3,g1)
    c: PointOnObject(g3,g5)
    c: Vertical(g5)
    c: PointOnObject(g5,g0)
    c: PointOnObject(g5,g3)
    c: DistanceY(g5) = -1.3
FEATURE [PartDesign::Revolution] Revolution  label="contact-master"
  Angle = 360
  Axis = (0,1,0)
  Base = (0,0,0)
  ReferenceAxis = -> Sketch021 [V_Axis]
  Reversed = true
  Sketch = -> Sketch021
FEATURE [App::DocumentObjectGroup] Group001  label="contacts-src"
  Group = -> [Fusion001001001003005,Pocket013,Revolution]
FEATURE [Part::Feature] Revolution001  label="contact-1"
  Placement = pos=(-18.9937,-24.85,5.7) rot=(0,0,1;0rad)
  shape: bbox 4.113 x 1.3 x 4.113 mm, 4 faces (baked)
FEATURE [Part::Feature] Revolution002  label="contact-2"
  Placement = pos=(-6.73125,-24.85,5.7) rot=(0,0,1;0rad)
  shape: bbox 4.113 x 1.3 x 4.113 mm, 4 faces (baked)
FEATURE [Part::Feature] Revolution003  label="contact-3"
  Placement = pos=(5.53125,-24.85,5.7) rot=(0,0,1;0rad)
  shape: bbox 4.113 x 1.3 x 4.113 mm, 4 faces (baked)
FEATURE [Part::Feature] Revolution004  label="contact-4"
  Placement = pos=(-6.73125,-24.85,-7.6) rot=(0,0,1;0rad)
  shape: bbox 4.113 x 1.3 x 4.113 mm, 4 faces (baked)
FEATURE [Part::Feature] Revolution005  label="contact-5"
  Placement = pos=(17.7937,-24.85,-7.6) rot=(0,0,1;0rad)
  shape: bbox 4.113 x 1.3 x 4.113 mm, 4 faces (baked)
FEATURE [Part::Feature] Revolution006  label="contact-6"
  Placement = pos=(17.7937,24.85,5.7) rot=(0,0,1;3.14159rad)
  shape: bbox 4.113 x 1.3 x 4.113 mm, 4 faces (baked)
FEATURE [Part::Feature] Revolution007  label="contact-7"
  Placement = pos=(-6.73125,24.85,5.7) rot=(0,0,1;3.14159rad)
  shape: bbox 4.113 x 1.3 x 4.113 mm, 4 faces (baked)
FEATURE [Part::Feature] Revolution008  label="contact-8"
  Placement = pos=(5.53125,24.85,-7.6) rot=(0,0,1;3.14159rad)
  shape: bbox 4.113 x 1.3 x 4.113 mm, 4 faces (baked)
FEATURE [Part::Feature] Revolution009  label="contact-9"
  Placement = pos=(-18.9937,24.85,-7.6) rot=(0,0,1;3.14159rad)
  shape: bbox 4.113 x 1.3 x 4.113 mm, 4 faces (baked)
FEATURE [Part::Compound] Compound001  label="contact-front"
  Links = -> [Revolution001,Revolution004,Revolution002,Revolution003,Revolution005,Revolution006,Revolution008,Revolution009,Revolution007]
FEATURE [Sketcher::SketchObject] Sketch023  label="top-body-2-sketch"
  ExternalGeometry = -> [Fusion]
  Placement = pos=(0,-26.65,0) rot=(1,0,0;1.5708rad)
  Support = -> Fusion [Face174]
  sketch-geometry (9):
    g0: LineSegment StartX=-15.3625 StartY=2.45 StartZ=0 EndX=-13.3625 EndY=2.45 EndZ=0
    g1: LineSegment StartX=-13.3625 StartY=2.45 StartZ=0 EndX=-13.3625 EndY=0 EndZ=0
    g2: LineSegment StartX=-13.3625 StartY=0 StartZ=0 EndX=-15.3625 EndY=0 EndZ=0
    g3: LineSegment StartX=-15.3625 StartY=0 StartZ=0 EndX=-15.3625 EndY=2.45 EndZ=0
    g4: LineSegment [constr] StartX=-12.2625 StartY=2.45 StartZ=0 EndX=-12.2625 EndY=0 EndZ=0
    g5: LineSegment StartX=-11.1625 StartY=2.45 StartZ=0 EndX=-9.1625 EndY=2.45 EndZ=0
    g6: LineSegment StartX=-9.1625 StartY=2.45 StartZ=0 EndX=-9.1625 EndY=0 EndZ=0
    g7: LineSegment StartX=-9.1625 StartY=0 StartZ=0 EndX=-11.1625 EndY=0 EndZ=0
    g8: LineSegment StartX=-11.1625 StartY=0 StartZ=0 EndX=-11.1625 EndY=2.45 EndZ=0
  constraints (26):
    c: Coincident(g0,g1)
    c: Coincident(g1,g2)
    c: Coincident(g2,g3)
    c: Coincident(g3,g0)
    c: Horizontal(g0)
    c: Horizontal(g2)
    c: Vertical(g1)
    c: Vertical(g3)
    c: Vertical(g4)
    c: PointOnObject(g4,g-1)
    c: PointOnObject(g1,g-1)
    c: Coincident(g5,g6)
    c: Coincident(g6,g7)
    c: Coincident(g7,g8)
    c: Coincident(g8,g5)
    c: Horizontal(g5)
    c: Horizontal(g7)
    c: Vertical(g6)
    c: Vertical(g8)
    c: Symmetric(g5,g0,g4)
    c: Symmetric(g6,g2,g4)
    c: DistanceX(g0) = 2
    c: PointOnObject(g0,g-3)
    c: Symmetric(g-3,g-3,g4)
    c: PointOnObject(g4,g-3)
    c: DistanceX(g0,g-3) = 0.2
FEATURE [PartDesign::Pocket] Pocket025  label="top-body-2"
  Length = 3.8
  Sketch = -> Sketch023
  Type = 0
FEATURE [Sketcher::SketchObject] Sketch013  label="top-body-3-sketch"
  ExternalGeometry = -> [Pocket025]
  Placement = pos=(0,26.65,0) rot=(0,0.707107,0.707107;3.14159rad)
  Support = -> Pocket025 [Face152]
  sketch-geometry (3):
    g0: LineSegment [constr] StartX=-12.2625 StartY=8.95 StartZ=0 EndX=-12.2625 EndY=2.45 EndZ=0
    g1: Circle CenterX=-14.7125 CenterY=2.45 CenterZ=0 NormalX=0 NormalY=0 NormalZ=1 Radius=0.95
    g2: Circle CenterX=-9.8125 CenterY=2.45 CenterZ=0 NormalX=0 NormalY=0 NormalZ=1 Radius=0.95
  constraints (9):
    c: Vertical(g0)
    c: Radius(g1) = 0.95
    c: Equal(g1,g2)
    c: Symmetric(g1,g2,g0)
    c: DistanceX(g1,g2) = 4.9
    c: PointOnObject(g0,g-3)
    c: Symmetric(g-3,g-3,g0)
    c: PointOnObject(g1,g-3)
    c: PointOnObject(g0,g-4)
FEATURE [PartDesign::Pocket] Pocket026  label="top-body-3"
  Length = 3
  Sketch = -> Sketch013
  Type = 0
FEATURE [Part::MultiFuse] Fusion001001001003006  label="top-body-4"
  Shapes = -> [Pocket026,Fusion001001001002]
FEATURE [Part::Chamfer] Chamfer002  label="top-half"
  Base = -> Fusion001001001003006
  Edges = 4 edges r=0.4: [Edge422,Edge424,Edge426,Edge428]
  Placement = pos=(0,0,0.05) rot=(0,0,1;0rad)
FEATURE [Part::Feature] Chamfer002001  label="bottom-half"
  Placement = pos=(0,0,0.05) rot=(0,1,0;3.14159rad)
  shape: bbox 51.23 x 53.32 x 12.42 mm, 374 faces (baked)
FEATURE [Part::MultiFuse] Fusion001001001003007  label="battery-holder-final"
  Shapes = -> [Chamfer002,Chamfer002001]
FEATURE [App::DocumentObjectGroup] Group  label="battery-holder-src"
  Group = -> [Pad,Pocket,Pocket001,Pocket002,Pocket003,Pocket004,Pocket005,Pocket006,Pocket007,Pocket008,Pocket009,Fusion,Fusion001001001002,Pocket025,Pocket026,Fusion001001001003006,Chamfer002,Chamfer002001,Fusion001001001003007]
FEATURE [Part::Feature] Fusion001001001003007001  label="battery-holder-body"
  Placement = pos=(-0.596129,0,-0.986262) rot=(0,0,1;0rad)
  shape: bbox 51.23 x 53.32 x 24.83 mm, 751 faces, 2 solids (baked)
FEATURE [Part::Feature] Pocket020001  label="star-010"
  Placement = pos=(17.8938,0,0.5) rot=(-1,0,0;1.5708rad)
  shape: bbox 5.019 x 4.871 x 0.2 mm, 21 faces (baked)
FEATURE [Part::Feature] Pocket020001001  label="star-011"
  Placement = pos=(-18.9,0,0.5) rot=(-1,0,0;1.5708rad)
  shape: bbox 5.019 x 4.871 x 0.2 mm, 21 faces (baked)
FEATURE [Part::Feature] Revolution001001  label="contact-010"
  Placement = pos=(17.8938,0,-1.3) rot=(-1,0,0;1.5708rad)
  shape: bbox 4.113 x 4.113 x 1.3 mm, 4 faces (baked)
FEATURE [Part::Feature] Revolution001001001  label="contact-011"
  Placement = pos=(-19.1062,0,-1.3) rot=(-1,0,0;1.5708rad)
  shape: bbox 4.113 x 4.113 x 1.3 mm, 4 faces (baked)
FEATURE [Part::Compound] Compound002  label="unions"
  Links = -> [Pocket020001,Revolution001001001,Pocket020001001,Revolution001001]
FEATURE [Part::Helix] Helix  label="Helix-orig"
  Angle = 10
  Height = 9
  LocalCoord = 0
  Pitch = 2.25
  Radius = 3
  Style = 1
FEATURE [Part::Feature] Edge  label="seg-path-4"
  shape: bbox 9.397 x 2e-07 x 7.261 mm, 0 faces, 0 solids (baked)
FEATURE [Part::Feature] Edge001  label="seg-path-3"
  shape: bbox 2.13 x 2e-07 x 3.934 mm, 0 faces, 0 solids (baked)
FEATURE [Part::Part2DObjectPython] Circle  label="sect-5"  # Draft 2D object (typed FeaturePython)
  FirstAngle = 0
  LastAngle = 0
  MakeFace = false
  Placement = pos=(-16.0102,15.85,4.8119) rot=(0,0,1;0rad)
  Radius = 0.4
FEATURE [Part::Feature] Edge002  label="seg-path-1"
  shape: bbox 0.09663 x 2e-07 x 4.554 mm, 0 faces, 0 solids (baked)
FEATURE [Part::Feature] Edge003  label="seg-path-2"
  shape: bbox 1.544 x 2e-07 x 4.027 mm, 0 faces, 0 solids (baked)
FEATURE [Part::Part2DObjectPython] Circle001  label="sect-1"  # Draft 2D object (typed FeaturePython)
  FirstAngle = 0
  LastAngle = 0
  MakeFace = false
  Placement = pos=(-18.0462,24.85,-6.81515) rot=(0,0,1;0rad)
  Radius = 0.4
FEATURE [Part::Sweep] Sweep  label="seg-1"
  Frenet = false
  Sections = -> [Circle001]
  Solid = true
  Spine = -> Edge002 [Edge1]
  Transition = 1
FEATURE [Part::Part2DObjectPython] Circle002  label="sect-2"  # Draft 2D object (typed FeaturePython)
  FirstAngle = 0
  LastAngle = 0
  MakeFace = false
  Placement = pos=(-17.9496,24.85,-2.26136) rot=(0,0,1;0rad)
  Radius = 0.4
FEATURE [Part::Sweep] Sweep001  label="seg-2"
  Frenet = false
  Sections = -> [Circle002]
  Solid = true
  Spine = -> Edge003 [Edge1]
  Transition = 1
FEATURE [Part::Part2DObjectPython] Circle003  label="sect-3"  # Draft 2D object (typed FeaturePython)
  FirstAngle = 0
  LastAngle = 0
  MakeFace = false
  Placement = pos=(-14.2954,24.85,5.7) rot=(0,0,1;0rad)
  Radius = 0.4
FEATURE [Part::Sweep] Sweep002  label="seg-3"
  Frenet = false
  Sections = -> [Circle003]
  Solid = true
  Spine = -> Edge001 [Edge1]
  Transition = 1
FEATURE [Part::Part2DObjectPython] Circle004  label="sect-4"  # Draft 2D object (typed FeaturePython)
  FirstAngle = 0
  LastAngle = 0
  MakeFace = false
  Placement = pos=(-14.2954,24.85,5.7) rot=(0,0,1;0rad)
  Radius = 0.4
FEATURE [Part::Sweep] Sweep003  label="seg-4"
  Frenet = false
  Sections = -> [Circle004]
  Solid = true
  Spine = -> Edge [Edge1]
  Transition = 1
FEATURE [Part::Feature] Edge004  label="seg-path-6"
  Placement = pos=(-19,15.85,5.5) rot=(-0.192433,0.693891,0.693891;2.76137rad)
  shape: bbox 9.202 x 9 x 9.331 mm, 0 faces, 0 solids (baked)
FEATURE [Part::Feature] Edge005  label="seg-path-5"
  shape: bbox 5.561 x 2e-07 x 2.225 mm, 0 faces, 0 solids (baked)
FEATURE [Part::Sweep] Sweep004  label="seg-5"
  Frenet = false
  Sections = -> [Circle]
  Solid = true
  Spine = -> Edge005 [Edge1]
  Transition = 1
FEATURE [Part::Part2DObjectPython] Circle005  label="sect-006"  # Draft 2D object (typed FeaturePython)
  FirstAngle = 0
  LastAngle = 0
  MakeFace = false
  Placement = pos=(-22.9318,24.85,3.13755) rot=(0,0,1;0rad)
  Radius = 0.4
FEATURE [Part::Sweep] Sweep005  label="seg-6"
  Frenet = true
  Sections = -> [Circle005]
  Solid = true
  Spine = -> Edge004 [Edge1]
  Transition = 1
FEATURE [Part::Compound] Compound003  label="spring-wire-1"
  Links = -> [Sweep,Sweep002,Sweep005,Sweep001,Sweep003,Sweep004]
  Placement = pos=(0,-0.4,0) rot=(0,0,1;0rad)
FEATURE [App::DocumentObjectGroup] Group003  label="spring-wire-1-src"
  Group = -> [Edge,Edge001,Edge002,Edge003,Edge004,Edge005]
FEATURE [Part::Part2DObjectPython] Arc002  label="path"  # Draft 2D object (typed FeaturePython)
  FirstAngle = -100.761
  LastAngle = 91.1171
  MakeFace = false
  Placement = pos=(-18.9938,-15.85,-7.6) rot=(-1,0,0;1.5708rad)
  Radius = 3.09938
  Support = -> Compound001
FEATURE [Part::Feature] Wire001  label="path003"
  shape: bbox 8.132 x 2e-07 x 1.765 mm, 0 faces, 0 solids (baked)
FEATURE [Part::Part2DObjectPython] Circle006  label="sect"  # Draft 2D object (typed FeaturePython)
  FirstAngle = 0
  LastAngle = 0
  MakeFace = false
  Placement = pos=(-19.0542,-15.85,-10.6988) rot=(0.57735,0.57735,0.57735;2.0944rad)
  Radius = 0.4
FEATURE [Part::Sweep] Sweep006  label="seg"
  Frenet = true
  Sections = -> [Circle006]
  Solid = true
  Spine = -> Arc002 [Edge1]
  Transition = 1
FEATURE [Part::Part2DObjectPython] Circle007  label="sect001"  # Draft 2D object (typed FeaturePython)
  FirstAngle = 0
  LastAngle = 0
  MakeFace = false
  Placement = pos=(-19.5724,-15.85,-4.55512) rot=(0.57735,0.57735,0.57735;2.0944rad)
  Radius = 0.4
FEATURE [Part::Feature] Edge006  label="path001"
  Placement = pos=(-19,-15.85,-7.5) rot=(-0.503588,0.610901,-0.610901;4.07462rad)
  shape: bbox 9.304 x 9 x 9.456 mm, 0 faces, 0 solids (baked)
FEATURE [Part::Feature] Edge007  label="path002"
  shape: bbox 8.497 x 2e-07 x 9.289 mm, 0 faces, 0 solids (baked)
FEATURE [Part::Sweep] Sweep007  label="seg001"
  Frenet = true
  Sections = -> [Circle007]
  Solid = true
  Spine = -> Edge006 [Edge1]
  Transition = 1
FEATURE [Part::Part2DObjectPython] Circle008  label="sect002"  # Draft 2D object (typed FeaturePython)
  FirstAngle = 0
  LastAngle = 0
  MakeFace = false
  Placement = pos=(-19.8752,-24.85,-2.99733) rot=(0.57735,0.57735,0.57735;2.0944rad)
  Radius = 0.4
FEATURE [Part::Sweep] Sweep008  label="seg002"
  Frenet = true
  Sections = -> [Circle008]
  Solid = true
  Spine = -> Edge007 [Edge1]
  Transition = 1
FEATURE [Part::Part2DObjectPython] Circle009  label="sect003"  # Draft 2D object (typed FeaturePython)
  FirstAngle = 0
  LastAngle = 0
  MakeFace = false
  Placement = pos=(-15.1835,-24.85,-10.3283) rot=(0,1,0;0.810632rad)
  Radius = 0.4
  Support = -> Sweep008
FEATURE [Part::Sweep] Sweep009  label="seg003"
  Frenet = true
  Sections = -> [Circle009]
  Solid = true
  Spine = -> Wire001 [Edge2]
  Transition = 1
FEATURE [Part::Compound] Compound004  label="spring-wire-2"
  Links = -> [Sweep006,Sweep008,Sweep007,Sweep009]
  Placement = pos=(0,0.4,0) rot=(0,0,1;0rad)
FEATURE [App::DocumentObjectGroup] Group004  label="spring-wire-2-src"
  Group = -> [Arc002,Wire001,Edge006,Edge007]
FEATURE [Part::Feature] Compound005  label="spring-wire-003"
  Placement = pos=(0,0.4,0) rot=(0,0,1;0rad)
  shape: bbox 18.88 x 9.936 x 14.16 mm, 13 faces, 4 solids (baked)
FEATURE [Part::Mirroring] Part__Mirroring003  label="spring-wire-003 (Mirror #4)"
  Base = (0,0,0)
  Normal = (0,1,0)
  Placement = pos=(12.5,0,0) rot=(0,0,1;0rad)
  Source = -> Compound005
FEATURE [Part::Feature] Compound006  label="spring-wire-004"
  Placement = pos=(24.5,0.4,0) rot=(0,0,1;0rad)
  shape: bbox 18.88 x 9.936 x 14.16 mm, 13 faces, 4 solids (baked)
FEATURE [Part::Feature] Compound003001  label="spring-wire-005"
  Placement = pos=(-1.15,-0.4,-2) rot=(0,1,0;3.14159rad)
  shape: bbox 13.6 x 9.801 x 20 mm, 18 faces, 6 solids (baked)
FEATURE [Part::Feature] Compound004001  label="spring-wire-006"
  Placement = pos=(-1.2,0.4,-2) rot=(0,1,0;3.14159rad)
  shape: bbox 18.88 x 9.936 x 14.16 mm, 13 faces, 4 solids (baked)
FEATURE [Part::Mirroring] Part__Mirroring004  label="spring-wire-007 (Mirror #5)"
  Base = (0,0,0)
  Normal = (0,1,0)
  Placement = pos=(-12.2,0,0) rot=(0,0,1;0rad)
  Source = -> Compound004001
FEATURE [Part::Feature] Wire  label="path-7"
  shape: bbox 9.253 x 9.316 x 9 mm, 0 faces, 0 solids (baked)
FEATURE [App::DocumentObjectGroup] Group002  label="spring-src"
  Group = -> [Helix,Group003,Group004,Wire]
FEATURE [Sketcher::SketchObject] Sketch024  label="spring-7-sketch"
  Placement = pos=(-2.68064,0,0) rot=(1,0,0;1.5708rad)
  sketch-geometry (1):
    g0: Circle CenterX=5.68064 CenterY=0 CenterZ=0 NormalX=0 NormalY=0 NormalZ=1 Radius=0.4
  constraints (2):
    c: PointOnObject(g0,g-1)
    c: Radius(g0) = 0.4
FEATURE [Part::Sweep] Sweep010  label="spring-8"
  Frenet = true
  Placement = pos=(-6.8,-15.4,5.8) rot=(1,0,0;1.5708rad)
  Sections = -> [Sketch024]
  Solid = true
  Spine = -> Wire
  Transition = 1
FEATURE [Part::Feature] Compound004002  label="spring-wire-006-2"
  Placement = pos=(-1.2,0.4,-2) rot=(0,1,0;3.14159rad)
  shape: bbox 18.88 x 9.936 x 14.16 mm, 13 faces, 4 solids (baked)
FEATURE [Part::Compound] Compound004003  label="springs"
  Links = -> [Compound003,Compound004,Part__Mirroring003,Compound006,Sweep010,Compound004002,Compound003001,Part__Mirroring004]
FEATURE [Part::Feature] Wire002  label="wire+_path"
  shape: bbox 2.029 x 8.6 x 5.744 mm, 0 faces, 0 solids (baked)
FEATURE [Sketcher::SketchObject] Sketch025  label="wire+_section-sketch"
  Placement = pos=(-15.0648,-33.45,-0.0439654) rot=(1,0,0;1.5708rad)
  sketch-geometry (1):
    g0: Circle CenterX=0 CenterY=0 CenterZ=0 NormalX=0 NormalY=0 NormalZ=1 Radius=0.75
  constraints (2):
    c: Coincident(g0,g-1)
    c: Radius(g0) = 0.75
FEATURE [Part::Sweep] Sweep011  label="wire+"
  Frenet = true
  Sections = -> [Sketch025]
  Solid = true
  Spine = -> Wire002
  Transition = 1
FEATURE [Part::Chamfer] Chamfer002002  label="wire+_final"
  Base = -> Sweep011
  Edges = 1 edges r=0.3: [Edge2]
  Placement = pos=(0,0.6,0) rot=(0,0,1;0rad)
FEATURE [Sketcher::SketchObject] Sketch028  label="wire-section-sketch"
  Placement = pos=(-11.0021,-33.901,0.150141) rot=(1,0,0;1.5708rad)
  sketch-geometry (1):
    g0: Circle CenterX=0 CenterY=0 CenterZ=0 NormalX=0 NormalY=0 NormalZ=1 Radius=0.8
  constraints (2):
    c: Coincident(g0,g-1)
    c: Radius(g0) = 0.8
FEATURE [Part::Feature] Wire003  label="wire-_path"
  shape: bbox 3.271 x 9.051 x 5.55 mm, 0 faces, 0 solids (baked)
FEATURE [Part::Sweep] Sweep012  label="wire-"
  Frenet = true
  Sections = -> [Sketch028]
  Solid = true
  Spine = -> Wire003
  Transition = 1
FEATURE [Part::Chamfer] Chamfer002003  label="wire-_final"
  Base = -> Sweep012
  Edges = 1 edges r=0.5: [Edge2]
  Placement = pos=(0,0.5,0) rot=(0,0,1;0rad)
FEATURE [App::DocumentObjectGroup] Group005  label="wire-src"
  Group = -> [Wire002,Chamfer002002,Wire003,Chamfer002003]
FEATURE [Part::Feature] Chamfer002004  label="wire+001"
  Placement = pos=(0,0.6,0) rot=(0,0,1;0rad)
  shape: bbox 3.754 x 9.624 x 6.726 mm, 8 faces (baked)
FEATURE [Part::Feature] Chamfer002005  label="wire-001"
  Placement = pos=(0,0.5,0) rot=(0,0,1;0rad)
  shape: bbox 4.44 x 10.17 x 7.089 mm, 8 faces (baked)
FEATURE [Part::Compound] Compound004004  label="wires"
  Links = -> [Chamfer002004,Chamfer002005]
FEATURE [Part::Feature] Chamfer002006  label="Battery-1"
  Placement = pos=(-19,21,5.7) rot=(1,0,0;1.5708rad)
  shape: bbox 11.26 x 44.5 x 11.26 mm, 17 faces (baked)
FEATURE [Part::Feature] Chamfer  label="Battery-2"
  Placement = pos=(-6.7,-20.9,5.7) rot=(-1,0,0;1.5708rad)
  shape: bbox 11.26 x 44.5 x 11.26 mm, 17 faces (baked)
FEATURE [Part::Feature] Chamfer002007  label="Battery-003"
  Placement = pos=(5.5,21,5.7) rot=(1,0,0;1.5708rad)
  shape: bbox 11.26 x 44.5 x 11.26 mm, 17 faces (baked)
FEATURE [Part::Feature] Chamfer002008  label="Battery-004"
  Placement = pos=(17.8,-20.9,5.7) rot=(-1,0,0;1.5708rad)
  shape: bbox 11.26 x 44.5 x 11.26 mm, 17 faces (baked)
FEATURE [Part::Feature] Chamfer002009  label="Battery-005"
  Placement = pos=(17.8,21,-7.5) rot=(0,0.707107,-0.707107;3.14159rad)
  shape: bbox 11.26 x 44.5 x 11.26 mm, 17 faces (baked)
FEATURE [Part::Feature] Chamfer002010  label="Battery-006"
  Placement = pos=(5.5,-20.9,-7.5) rot=(0,0.707107,0.707107;3.14159rad)
  shape: bbox 11.26 x 44.5 x 11.26 mm, 17 faces (baked)
FEATURE [Part::Feature] Chamfer002011  label="Battery-007"
  Placement = pos=(-19,-20.9,-7.5) rot=(0,0.707107,0.707107;3.14159rad)
  shape: bbox 11.26 x 44.5 x 11.26 mm, 17 faces (baked)
FEATURE [Part::Feature] Chamfer002012  label="Battery-008"
  Placement = pos=(-6.7,21,-7.5) rot=(0,0.707107,-0.707107;3.14159rad)
  shape: bbox 11.26 x 44.5 x 11.26 mm, 17 faces (baked)
FEATURE [Part::Compound] Compound004005  label="batteries"
  Links = -> [Chamfer002006,Chamfer002010,Chamfer002009,Chamfer,Chamfer002008,Chamfer002012,Chamfer002011,Chamfer002007]
FEATURE [Part::Compound] Compound004006  label="battery-holder"
  Links = -> [Compound004004,Compound004003,Compound002,Fusion001001001003007001,Compound001,Compound]
